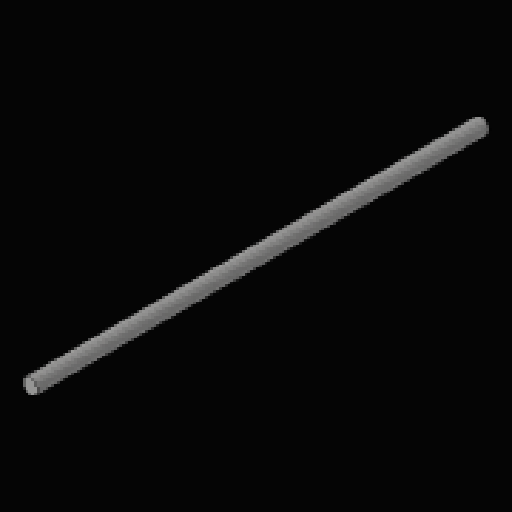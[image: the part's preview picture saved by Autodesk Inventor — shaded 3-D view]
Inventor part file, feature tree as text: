
AUTODESK INVENTOR PART (.ipt)
format: ipt  version: 2023.2 (Build 272271030, 271C)  size: 89,088 bytes
history: native  units: mm
features: extrude x1, thread x1, sketch x1
ambient origin geometry x8: Origin, YZ Plane, XZ Plane, XY Plane, X Axis, Y Axis, Z Axis, Center Point
bodies: Solid1 (feature_tree)
feature tree (3):
  extrude  "Extrusion1"  Depth=90.0mm TaperAngle=0.0deg
  thread  "Thread1"  [1 undecoded]
  sketch  "Sketch1"  dims[d0=3.0mm d1=90.0mm d2=0.0mm d3=90.0mm d4=0.0mm]
note: 1 required parameter value undecoded (feature->parameter linkage not recoverable at this tier; creation-order binding heuristic only, values carry confidence <= 0.55)
